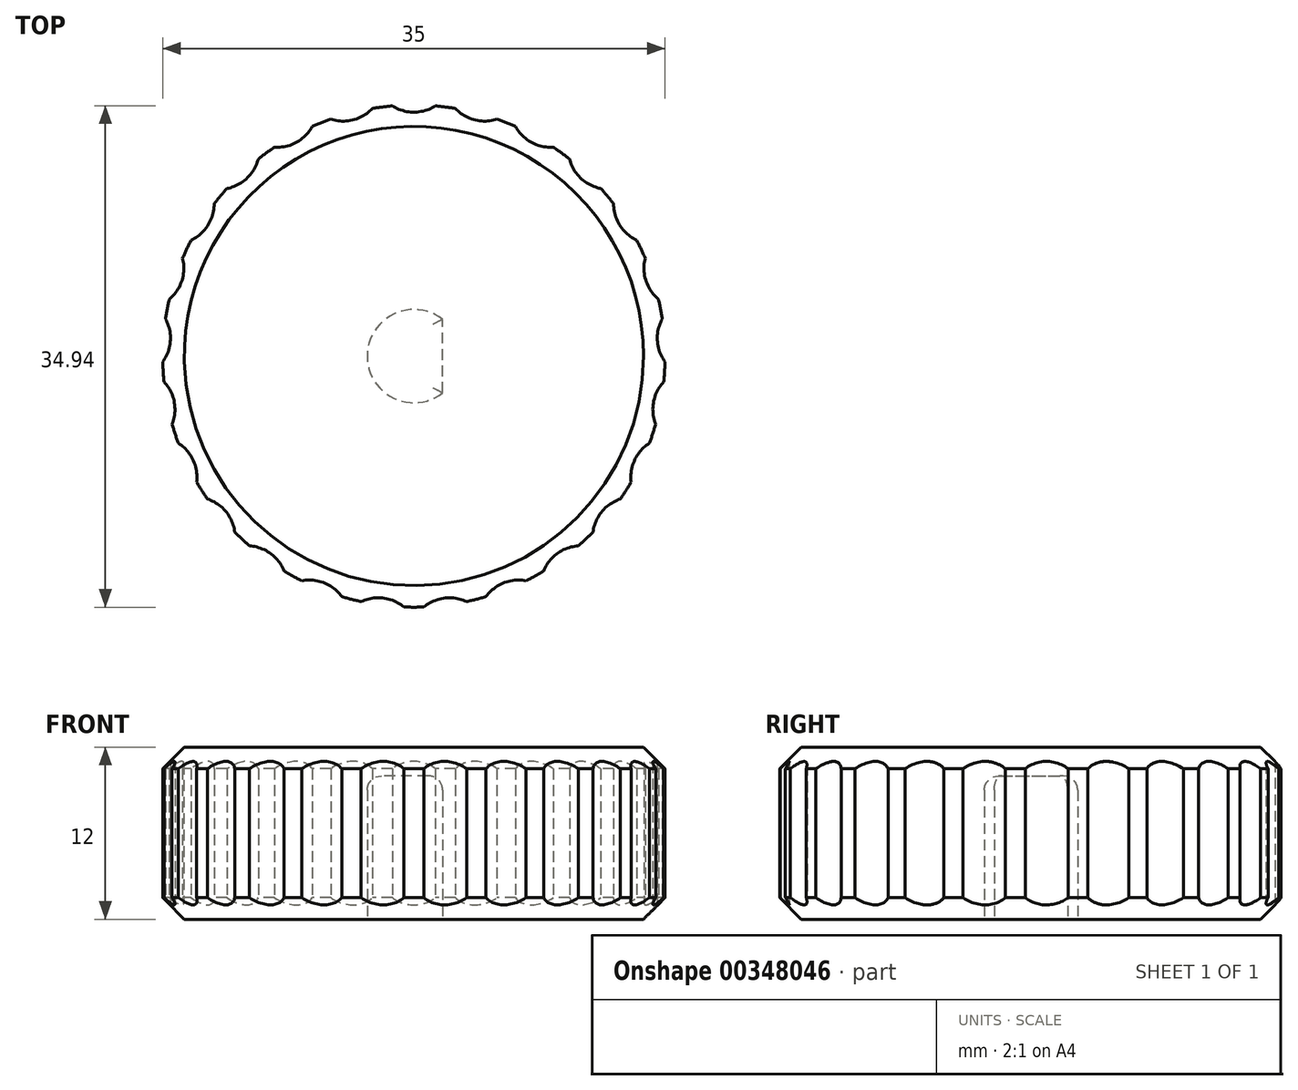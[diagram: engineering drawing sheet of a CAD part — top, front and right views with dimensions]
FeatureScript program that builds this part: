
annotation { "Feature Type Name" : "Feature", "Feature Type Description" : "" }
export const myFeature = defineFeature(function(context is Context, id is Id, definition is map)
    precondition{}
    {
        {
            assignVariable(context, id + "F0", {"name" : "KnobHeight", "anyValue" : 12});
        }
        {
            assignVariable(context, id + "F1", {"name" : "NotchCount", "anyValue" : 25});
        }
        {
            var Q0;
            Q0=qCreatedBy(makeId("Top.planeOp"),FACE);
            var sketch = newSketch(context, id + "F2", { "sketchPlane" : qUnion([Q0])});
            skCircle(sketch, "E0", {"center": v(0, 0) * mm, "radius": 17.5 * mm});
            skCircle(sketch, "E1", {"center": v(0, 0) * mm, "radius": 15 * mm});
            skArc(sketch, "E2", {"start": v(-1.5, 17.44) * mm, "mid": v(0, 17) * mm, "end": v(1.5, 17.44) * mm});
            skCircle(sketch, "E3", {"center": v(0, 0) * mm, "radius": 14 * mm});
            skSolve(sketch);
        }
        {
            var Q0;
            Q0=makeQuery(id+"F2.imprint","IMPRINT",FACE,{"disambiguationData":[TD([[makeQuery(id+"F2.imprint","IMPRINT",EDGE,{"derivedFrom":sQuery(id+"F2.wireOp",EDGE,"E1")}),-1.0]])]});
            var Q1;
            {var subQ0=sQuery(id+"F2.wireOp",EDGE,"cUZMMoAc-PTST-COai-DZw3-MpeYMIDPBgKU");var subQ1=sQuery(id+"F2.wireOp",EDGE,"E0");var subQ2=makeQuery(id+"F2.imprint","INTERSECT",VERTEX,{"disambiguationData":[OD(0.0)],"derivedFrom":[subQ1,subQ0]});Q1=makeQuery(id+"F2.imprint","IMPRINT",FACE,{"disambiguationData":[TD([[makeQuery(id+"F2.imprint","IMPRINT",EDGE,{"disambiguationData":[TD([[subQ2,1.0]])],"derivedFrom":subQ1}),1.0]])]});}
            extrude(context, id + "F3", {"entities" : qUnion([Q0, Q1]), "depth" : (getVariable(context, 'KnobHeight')) * mm});
        }
        {
            var Q0;
            Q0=makeQuery(id+"F2.imprint","IMPRINT",FACE,{"disambiguationData":[TD([[makeQuery(id+"F2.imprint","IMPRINT",EDGE,{"derivedFrom":sQuery(id+"F2.wireOp",EDGE,"E1")}),1.0]])]});
            extrude(context, id + "F4", {"entities" : qUnion([Q0]), "operationType" : NewBodyOperationType.ADD, "depth" : (getVariable(context, 'KnobHeight')) * mm, "hasSecondDirection" : true, "secondDirectionOppositeDirection" : false, "secondDirectionDepth" : (getVariable(context, 'KnobHeight') - 1) * mm});
        }
        {
            var Q0;
            Q0=makeQuery(id+"F2.imprint","IMPRINT",FACE,{"disambiguationData":[TD([[makeQuery(id+"F2.imprint","IMPRINT",EDGE,{"derivedFrom":sQuery(id+"F2.wireOp",EDGE,"E1")}),1.0]])]});
            extrude(context, id + "F5", {"entities" : qUnion([Q0]), "operationType" : NewBodyOperationType.ADD, "depth" : 1 * mm});
        }
        {
            var Q0;
            Q0=makeQuery(id+"F2.imprint","IMPRINT",FACE,{"disambiguationData":[TD([[makeQuery(id+"F2.imprint","IMPRINT",EDGE,{"derivedFrom":sQuery(id+"F2.wireOp",EDGE,"E3")}),1.0]])]});
            extrude(context, id + "F6", {"entities" : qUnion([Q0]), "depth" : (getVariable(context, 'KnobHeight')) * mm});
        }
        {
            var Q0;
            Q0=makeQuery(id+"F3.opExtrude","CAP_EDGE",EDGE,{"disambiguationData":[OSD([sQuery(id+"F2.wireOp",EDGE,"E0")])],"isStart":false});
            var Q1;
            Q1=makeQuery(id+"F3.opExtrude","CAP_EDGE",EDGE,{"disambiguationData":[OSD([sQuery(id+"F2.wireOp",EDGE,"E0")])],"isStart":true});
            chamfer(context, id + "F7", {"entities" : qUnion([Q0, Q1]), "width" : 1.5 * mm, "tangentPropagation" : true});
        }
        {
            var Q0;
            {var subQ0=sQuery(id+"F2.wireOp",EDGE,"cUZMMoAc-PTST-COai-DZw3-MpeYMIDPBgKU");var subQ1=sQuery(id+"F2.wireOp",EDGE,"E0");var subQ2=makeQuery(id+"F2.imprint","INTERSECT",VERTEX,{"disambiguationData":[OD(0.0)],"derivedFrom":[subQ1,subQ0]});Q0=makeQuery(id+"F2.imprint","IMPRINT",FACE,{"disambiguationData":[TD([[makeQuery(id+"F2.imprint","IMPRINT",EDGE,{"disambiguationData":[TD([[subQ2,1.0]])],"derivedFrom":subQ1}),1.0]])]});}
            extrude(context, id + "F8", {"entities" : qUnion([Q0]), "depth" : 25 * mm});
        }
        {
            var Q0;
            Q0=makeQuery(id+"F8.opExtrude","SWEPT_BODY",BODY,{"disambiguationData":[OSD([sQuery(id+"F2.wireOp",EDGE,"E0"),sQuery(id+"F2.wireOp",EDGE,"cUZMMoAc-PTST-COai-DZw3-MpeYMIDPBgKU")])]});
            var Q1;
            Q1=sQuery(id+"F2.wireOp",EDGE,"E0");
            circularPattern(context, id + "F9", {"operationType" : NewBodyOperationType.REMOVE, "entities" : qUnion([Q0]), "axis" : qUnion([Q1]), "angle" : 360 * degree, "instanceCount" : getVariable(context, 'NotchCount'), "equalSpace" : true});
        }
        {
            var Q0;
            Q0=makeQuery(id+"F2.imprint","IMPRINT",FACE,{"disambiguationData":[TD([[makeQuery(id+"F2.imprint","IMPRINT",EDGE,{"derivedFrom":sQuery(id+"F2.wireOp",EDGE,"E1")}),1.0]])]});
            extrude(context, id + "F10", {"entities" : qUnion([Q0]), "operationType" : NewBodyOperationType.ADD, "depth" : (getVariable(context, 'KnobHeight') - 1) * mm, "hasSecondDirection" : true, "secondDirectionOppositeDirection" : false, "secondDirectionDepth" : 1 * mm});
        }
        {
            var Q0;
            Q0=makeQuery(id+"F6.opExtrude","CAP_FACE",FACE,{"disambiguationData":[OSD([sQuery(id+"F2.wireOp",EDGE,"E3")])],"isStart":true});
            var sketch = newSketch(context, id + "F11", { "sketchPlane" : qUnion([Q0])});
            skCircle(sketch, "E4", {"center": v(0, 0) * mm, "radius": 3.25 * mm});
            skLineSegment(sketch, "E5", {"start": v(2, 2.56) * mm, "end": v(2, -2.56) * mm});
            skSolve(sketch);
        }
        {
            var Q0;
            {var subQ0=sQuery(id+"F11.wireOp",EDGE,"E5");Q0=makeQuery(id+"F11.imprint","IMPRINT",FACE,{"disambiguationData":[TD([[makeQuery(id+"F11.imprint","IMPRINT",EDGE,{"derivedFrom":subQ0}),-1.0]])]});}
            extrude(context, id + "F12", {"entities" : qUnion([Q0]), "operationType" : NewBodyOperationType.REMOVE, "oppositeDirection" : true, "depth" : 10 * mm});
        }
        {
            var Q0;
            Q0=makeQuery(id+"F12.boolean.opBoolean","COPY",EDGE,{"derivedFrom":makeQuery(id+"F12.opExtrude","CAP_EDGE",EDGE,{"disambiguationData":[OSD([sQuery(id+"F11.wireOp",EDGE,"E4")])],"isStart":true})});
            var Q1;
            Q1=makeQuery(id+"F12.boolean.opBoolean","COPY",EDGE,{"derivedFrom":makeQuery(id+"F12.opExtrude","CAP_EDGE",EDGE,{"disambiguationData":[OSD([sQuery(id+"F11.wireOp",EDGE,"E5")])],"isStart":true})});
            var Q2;
            Q2=makeQuery(id+"F12.boolean.opBoolean","COPY",FACE,{"derivedFrom":makeQuery(id+"F12.opExtrude","CAP_FACE",FACE,{"disambiguationData":[OSD([sQuery(id+"F11.wireOp",EDGE,"E4"),sQuery(id+"F11.wireOp",EDGE,"E5")])],"isStart":false})});
            fillet(context, id + "F13", {"entities" : qUnion([Q0, Q1, Q2]), "radius" : 1 * mm, "tangentPropagation" : true, "allowEdgeOverflow" : false});
        }
    });
